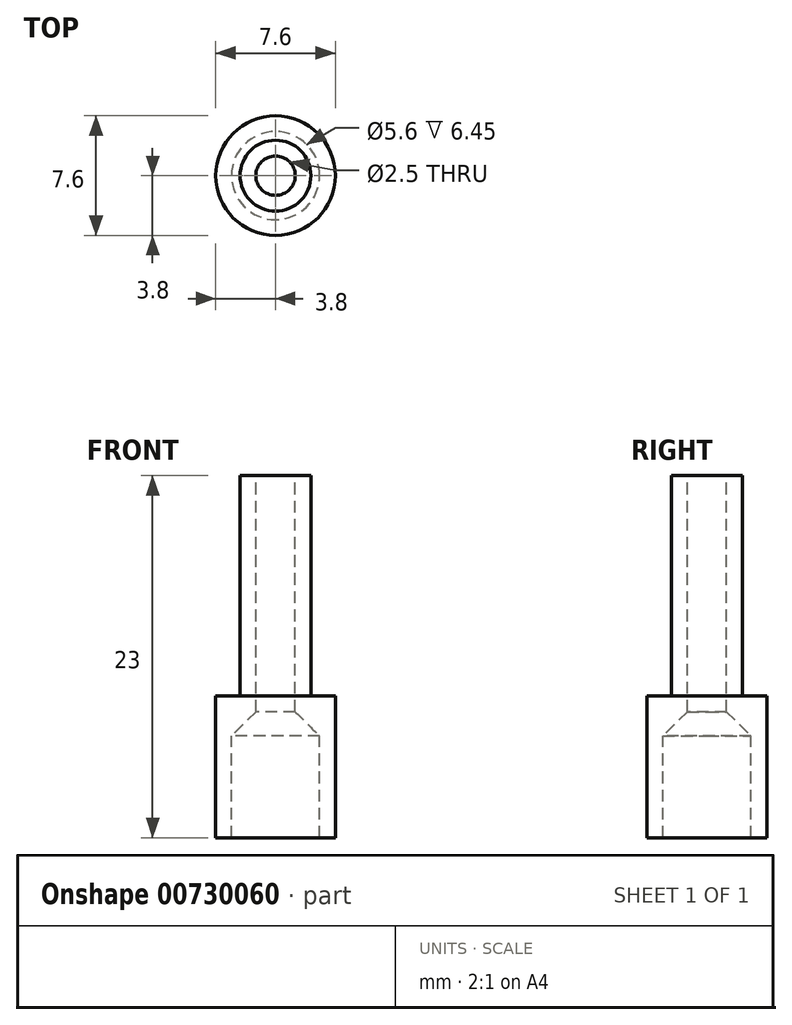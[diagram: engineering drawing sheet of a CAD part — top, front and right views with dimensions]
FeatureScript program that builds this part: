
annotation { "Feature Type Name" : "Feature", "Feature Type Description" : "" }
export const myFeature = defineFeature(function(context is Context, id is Id, definition is map)
    precondition{}
    {
        {
            var Q0;
            Q0=qCreatedBy(makeId("Front.planeOp"),FACE);
            var sketch = newSketch(context, id + "F0", { "sketchPlane" : qUnion([Q0])});
            skLineSegment(sketch, "E0", {"start": v(-2.8, 0) * mm, "end": v(-2.8, 8) * mm});
            skLineSegment(sketch, "E1", {"start": v(-2.8, 8) * mm, "end": v(-1.25, 8) * mm});
            skLineSegment(sketch, "E2", {"start": v(-1.25, 8) * mm, "end": v(-1.25, 23) * mm});
            skLineSegment(sketch, "E3", {"start": v(0, 23) * mm, "end": v(0, 0) * mm});
            skLineSegment(sketch, "E4", {"start": v(-4.8, 0) * mm, "end": v(-2.8, 0) * mm});
            skLineSegment(sketch, "E5", {"start": v(-1.25, 23) * mm, "end": v(-3.25, 23) * mm});
            skLineSegment(sketch, "E6", {"start": v(-4.6, 23) * mm, "end": v(-1.25, 23) * mm});
            skLineSegment(sketch, "E7", {"start": v(0, 0) * mm, "end": v(0, 23) * mm, "construction": true});
            skLineSegment(sketch, "E8.0", {"start": v(-2.25, 9) * mm, "end": v(-2.25, 23) * mm});
            skLineSegment(sketch, "E8.1", {"start": v(-3.8, 9) * mm, "end": v(-2.25, 9) * mm});
            skLineSegment(sketch, "E8.2", {"start": v(-3.8, 0) * mm, "end": v(-3.8, 9) * mm});
            skLineSegment(sketch, "E9", {"start": v(-1.25, 8) * mm, "end": v(-2.8, 6.45) * mm});
            skSolve(sketch);
        }
        {
            var Q0;
            Q0=makeQuery(id+"F0.imprint","IMPRINT",FACE,{"disambiguationData":[TD([[makeQuery(id+"F0.imprint","IMPRINT",EDGE,{"derivedFrom":sQuery(id+"F0.wireOp",EDGE,"E0")}),1.0]])]});
            var Q1;
            {var subQ0=sQuery(id+"F0.wireOp",EDGE,"E1");Q1=makeQuery(id+"F0.imprint","IMPRINT",FACE,{"disambiguationData":[TD([[makeQuery(id+"F0.imprint","IMPRINT",EDGE,{"derivedFrom":subQ0}),-1.0]])]});}
            var Q2;
            Q2=sQuery(id+"F0.wireOp",EDGE,"E3");
            revolve(context, id + "F1", {"surfaceOperationType" : NewSurfaceOperationType.NEW, "entities" : qUnion([Q0, Q1]), "axis" : qUnion([Q2]), "revolveType" : RevolveType.FULL});
        }
    });
